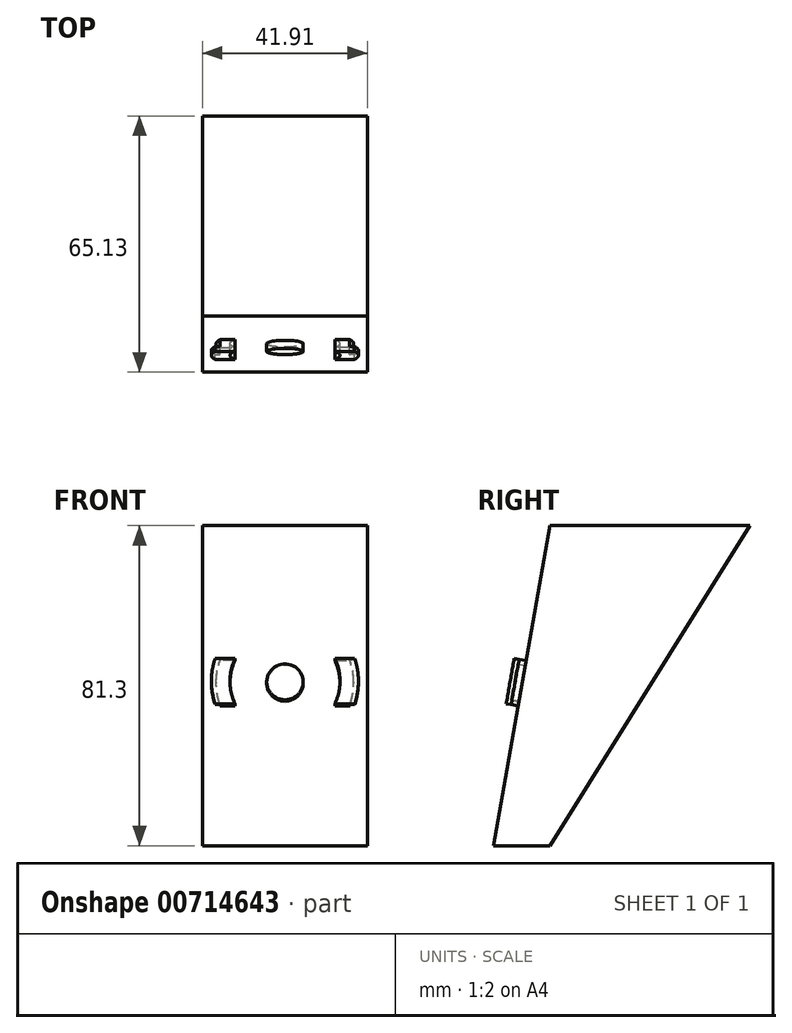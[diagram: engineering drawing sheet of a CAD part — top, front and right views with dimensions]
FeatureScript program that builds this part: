
annotation { "Feature Type Name" : "Feature", "Feature Type Description" : "" }
export const myFeature = defineFeature(function(context is Context, id is Id, definition is map)
    precondition{}
    {
        {
            var Q0;
            Q0=qCreatedBy(makeId("Right.planeOp"),FACE);
            var sketch = newSketch(context, id + "F0", { "sketchPlane" : qUnion([Q0])});
            skLineSegment(sketch, "E0", {"start": v(0, 0) * mm, "end": v(50.8, 0) * mm});
            skLineSegment(sketch, "E1", {"start": v(50.8, 0) * mm, "end": v(0, -81.3) * mm});
            skLineSegment(sketch, "E2", {"start": v(0, -81.3) * mm, "end": v(-14.33, -81.3) * mm});
            skLineSegment(sketch, "E3", {"start": v(-14.33, -81.3) * mm, "end": v(0, 0) * mm});
            skSolve(sketch);
        }
        {
            var Q0;
            Q0=makeQuery(id+"F0.imprint","IMPRINT",FACE,{"disambiguationData":[TD([[makeQuery(id+"F0.imprint","IMPRINT",EDGE,{"derivedFrom":sQuery(id+"F0.wireOp",EDGE,"E0")}),-1.0]])]});
            extrude(context, id + "F1", {"entities" : qUnion([Q0]), "oppositeDirection" : true, "depth" : 41.9 * mm, "offsetDistance" : 25.4 * mm});
        }
        {
            var Q0;
            Q0=makeQuery(id+"F1.opExtrude","SWEPT_FACE",FACE,{"disambiguationData":[OSD([sQuery(id+"F0.wireOp",EDGE,"E3")])]});
            var sketch = newSketch(context, id + "F2", { "sketchPlane" : qUnion([Q0])});
            skCircle(sketch, "E4", {"center": v(-20.96, -40.64) * mm, "radius": 4.64 * mm});
            skLineSegment(sketch, "E5", {"start": v(-41.91, -40.64) * mm, "end": v(0, -40.64) * mm, "construction": true});
            skCircle(sketch, "E6", {"center": v(-20.96, -40.64) * mm, "radius": 18.67 * mm, "construction": true});
            skCircle(sketch, "E7", {"center": v(-20.96, -40.64) * mm, "radius": 17.46 * mm, "construction": true});
            skCircle(sketch, "E8", {"center": v(-20.96, -40.64) * mm, "radius": 13.97 * mm, "construction": true});
            skArc(sketch, "E9", {"start": v(-8.27, -46.48) * mm, "mid": v(-6.98, -40.64) * mm, "end": v(-8.27, -34.8) * mm});
            skArc(sketch, "E10", {"start": v(-4.5, -46.48) * mm, "mid": v(-3.5, -40.64) * mm, "end": v(-4.5, -34.8) * mm});
            skArc(sketch, "E11", {"start": v(-3.22, -46.48) * mm, "mid": v(-2.29, -40.64) * mm, "end": v(-3.22, -34.8) * mm});
            skLineSegment(sketch, "E12", {"start": v(-8.27, -34.8) * mm, "end": v(-4.5, -34.8) * mm});
            skLineSegment(sketch, "E13", {"start": v(-4.5, -34.8) * mm, "end": v(-3.22, -34.8) * mm});
            skLineSegment(sketch, "E14", {"start": v(-3.22, -46.48) * mm, "end": v(-4.5, -46.48) * mm});
            skLineSegment(sketch, "E15", {"start": v(-4.5, -46.48) * mm, "end": v(-8.27, -46.48) * mm});
            skSolve(sketch);
        }
        {
            var Q0;
            Q0=makeQuery(id+"F2.imprint","IMPRINT",FACE,{"disambiguationData":[TD([[makeQuery(id+"F2.imprint","IMPRINT",EDGE,{"derivedFrom":sQuery(id+"F2.wireOp",EDGE,"E4")}),1.0]])]});
            extrude(context, id + "F3", {"entities" : qUnion([Q0]), "operationType" : NewBodyOperationType.ADD, "depth" : 2.03 * mm, "offsetDistance" : 25.4 * mm});
        }
        {
            var Q0;
            Q0=makeQuery(id+"F2.imprint","IMPRINT",FACE,{"disambiguationData":[TD([[makeQuery(id+"F2.imprint","IMPRINT",EDGE,{"derivedFrom":sQuery(id+"F2.wireOp",EDGE,"E9")}),-1.0]])]});
            var Q1;
            Q1=makeQuery(id+"F2.imprint","IMPRINT",FACE,{"disambiguationData":[TD([[makeQuery(id+"F2.imprint","IMPRINT",EDGE,{"derivedFrom":sQuery(id+"F2.wireOp",EDGE,"E10")}),-1.0]])]});
            extrude(context, id + "F4", {"entities" : qUnion([Q0, Q1]), "depth" : 3.05 * mm, "offsetDistance" : 25.4 * mm});
        }
        {
            var Q0;
            Q0=makeQuery(id+"F2.imprint","IMPRINT",FACE,{"disambiguationData":[TD([[makeQuery(id+"F2.imprint","IMPRINT",EDGE,{"derivedFrom":sQuery(id+"F2.wireOp",EDGE,"E10")}),-1.0]])]});
            extrude(context, id + "F5", {"entities" : qUnion([Q0]), "operationType" : NewBodyOperationType.REMOVE, "depth" : 1.78 * mm, "offsetDistance" : 25.4 * mm});
        }
        {
            var Q0;
            Q0=makeQuery(id+"F1.opExtrude","CAP_FACE",FACE,{"disambiguationData":[OSD([sQuery(id+"F0.wireOp",EDGE,"E0"),sQuery(id+"F0.wireOp",EDGE,"E1"),sQuery(id+"F0.wireOp",EDGE,"E2"),sQuery(id+"F0.wireOp",EDGE,"E3")])],"isStart":true});
            var Q1;
            Q1=makeQuery(id+"F1.opExtrude","CAP_FACE",FACE,{"disambiguationData":[OSD([sQuery(id+"F0.wireOp",EDGE,"E0"),sQuery(id+"F0.wireOp",EDGE,"E1"),sQuery(id+"F0.wireOp",EDGE,"E2"),sQuery(id+"F0.wireOp",EDGE,"E3")])],"isStart":false});
            cPlane(context, id + "F6", {"entities" : qUnion([Q0, Q1]), "cplaneType" : CPlaneType.MID_PLANE, "offset" : 25.4 * mm, "width" : 152.4 * mm, "height" : 152.4 * mm});
        }
        {
            var Q0;
            Q0=makeQuery(id+"F4.opExtrude","SWEPT_BODY",BODY,{"disambiguationData":[OSD([sQuery(id+"F2.wireOp",EDGE,"E9"),sQuery(id+"F2.wireOp",EDGE,"E11"),sQuery(id+"F2.wireOp",EDGE,"E12"),sQuery(id+"F2.wireOp",EDGE,"E13"),sQuery(id+"F2.wireOp",EDGE,"E14"),sQuery(id+"F2.wireOp",EDGE,"E15")])]});
            var Q1;
            Q1=qCreatedBy(id+"F6.planeOp",FACE);
            mirror(context, id + "F7", {"operationType" : NewBodyOperationType.ADD, "entities" : qUnion([Q0]), "mirrorPlane" : qUnion([Q1])});
        }
    });
